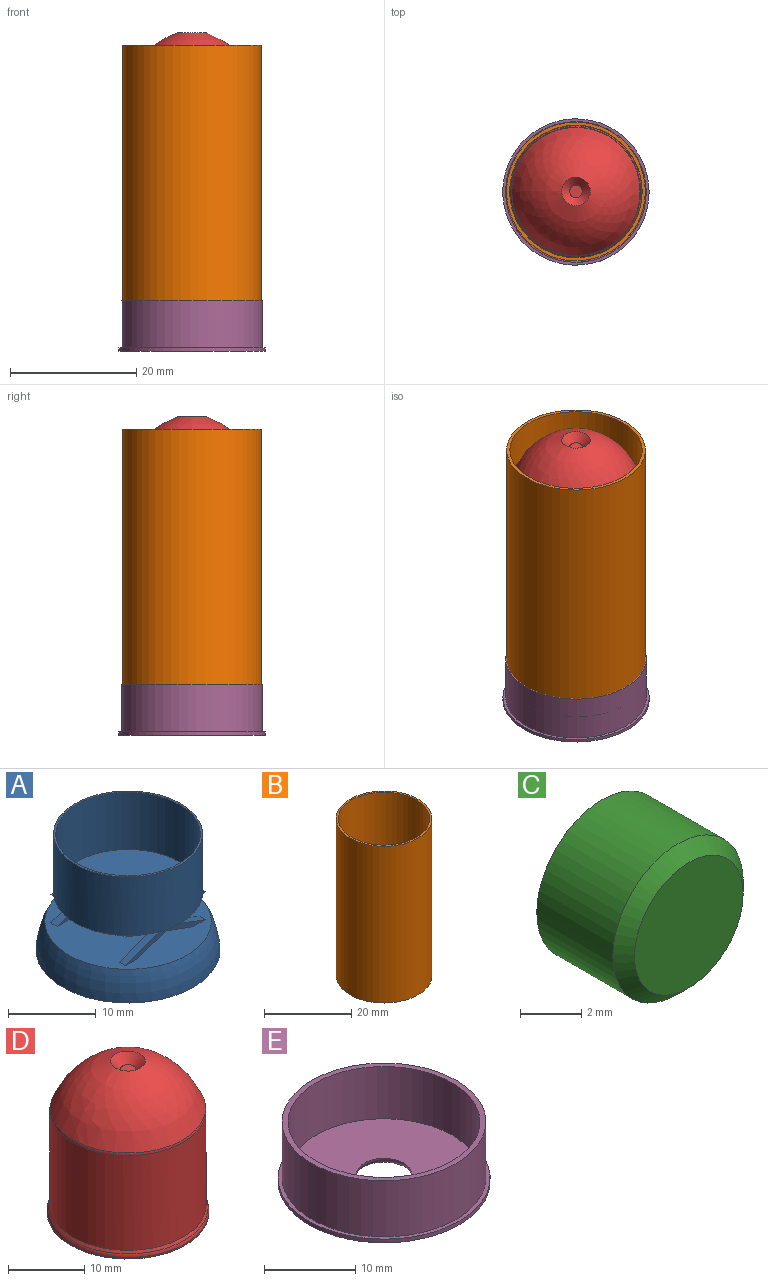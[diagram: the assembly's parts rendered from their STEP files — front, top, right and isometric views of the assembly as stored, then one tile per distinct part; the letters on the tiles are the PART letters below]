
ASSEMBLY  parts=5 mates=4
PART A: 40 faces, bbox 21x21x16.2 mm
  f0: plane 17.01x17.01mm, normal (0,0,-1), area 219.3mm2, adj f1,f6,f7,f8,f9,f10,f11,f12
  f1: cylinder r=8.5mm len=17mm, axis (0,0,1), area 437.9mm2, adj f0,f2,f3,f4,f5,f37
  f2: plane 0.45x0.43mm, normal (0,0,1), area 0.1mm2, adj f1,f8,f21
  f3: plane 0.45x0.43mm, normal (0,0,1), area 0.1mm2, adj f1,f8,f18
  f4: plane 0.46x0.43mm, normal (0,0,1), area 0.1mm2, adj f1,f12,f25
  f5: plane 0.45x0.43mm, normal (0,0,1), area 0.1mm2, adj f1,f12,f26
  f6: plane 4.43x1.63mm, normal (0.34,0,0.94), area 4.7mm2, adj f0,f7,f8,f9
  f7: plane 4.43x1.63mm, normal (-0.34,0,0.94), area 4.7mm2, adj f0,f6,f8,f9
  f8: plane 12.89x4mm, normal (0,1,0), area 15.2mm2, adj f0,f2,f3,f6,f7,f14,f17,f18
  f9: plane 12.9x4mm, normal (0,-1,0), area 14.8mm2, adj f0,f6,f7,f14,f17,f18,f19,f20
  f10: plane 4.43x1.63mm, normal (-0.34,0,0.94), area 4.7mm2, adj f0,f11,f12,f13
  f11: plane 4.43x1.63mm, normal (0.34,0,0.94), area 4.7mm2, adj f0,f10,f12,f13
  f12: plane 12.89x4mm, normal (0,-1,0), area 15.2mm2, adj f0,f4,f5,f10,f11,f14,f25,f26
  f13: plane 12.89x4mm, normal (0,1,0), area 14.8mm2, adj f0,f10,f11,f14,f25,f26,f27,f28
  f14: plane 19x18.95mm, normal (0,0,1), area 275.5mm2, adj f8,f9,f12,f13,f16,f17,f19,f20
  f15: plane 21x21mm, normal (0,0,-1), area 77.5mm2, adj f16,f23,f24,f35
  f16: torus R=0.21mm, axis (0,0,1), area 264.3mm2, adj f14,f15,f24
  f17: plane 5.45x2mm, normal (-0.34,0,0.94), area 5.8mm2, adj f8,f9,f14,f18
  f18: plane 5.46x2.01mm, normal (-0.34,0,-0.94), area 5.8mm2, adj f0,f3,f8,f9,f17
  f19: plane 4.45x1.63mm, normal (-0.34,0,-0.94), area 4.7mm2, adj f8,f9,f14,f20
  f20: plane 4.45x1.63mm, normal (0.34,0,-0.94), area 4.7mm2, adj f8,f9,f14,f19
  f21: plane 5.45x2mm, normal (0.34,0,-0.94), area 5.8mm2, adj f0,f2,f8,f9,f22
  f22: plane 5.45x2mm, normal (0.34,0,0.94), area 5.8mm2, adj f8,f9,f14,f21
  f23: plane 4x2mm, normal (1,0,0), area 8mm2, adj f14,f15,f24
  f24: cylinder r=9.5mm len=4mm, axis (0,0,1), area 8mm2, adj f15,f16,f23
  f25: plane 5.46x2.01mm, normal (0.34,0,-0.94), area 5.8mm2, adj f0,f4,f12,f13,f30
  f26: plane 5.45x2mm, normal (-0.34,0,-0.94), area 5.8mm2, adj f0,f5,f12,f13,f27
  f27: plane 5.45x2mm, normal (-0.34,0,0.94), area 5.8mm2, adj f12,f13,f14,f26
  f28: plane 4.45x1.63mm, normal (0.34,0,-0.94), area 4.7mm2, adj f12,f13,f14,f29
  f29: plane 4.45x1.63mm, normal (-0.34,0,-0.94), area 4.7mm2, adj f12,f13,f14,f28
  f30: plane 5.45x2mm, normal (0.34,0,0.94), area 5.8mm2, adj f12,f13,f14,f25
  f31: plane 10x1.01mm, normal (0,0,-1), area 10.1mm2, adj f9,f13,f32,f34
  f32: plane 10x0.45mm, normal (1,0,0), area 4.5mm2, adj f9,f13,f31,f33
  f33: plane 10x1.01mm, normal (0,0,1), area 10.1mm2, adj f9,f13,f32,f34
  f34: plane 10x0.45mm, normal (-1,0,0), area 4.5mm2, adj f9,f13,f31,f33
  f35: cylinder r=9.25mm len=18.5mm, axis (0,0,-1), area 116.2mm2, adj f15,f36
  f36: plane 18.5x18.5mm, normal (0,0,-1), area 268.8mm2, adj f35
  f37: plane 17x17mm, normal (0,0,1), area 13.2mm2, adj f1,f38
  f38: cylinder r=8.25mm len=16.5mm, axis (0,0,1), area 414.7mm2, adj f37,f39
  f39: plane 16.5x16.5mm, normal (0,0,1), area 213.8mm2, adj f38
PART B: 4 faces, bbox 22x22x44 mm
  f0: cylinder r=11mm len=44mm, axis (0,0,-1), area 3041.1mm2, adj f1,f2
  f1: plane 22x22mm, normal (0,0,1), area 33.8mm2, adj f0,f3
  f2: plane 22x22mm, normal (0,0,-1), area 33.8mm2, adj f0,f3
  f3: cylinder r=10.5mm len=44mm, axis (0,0,1), area 2902.8mm2, adj f1,f2
PART C: 4 faces, bbox 6x4x6 mm
  f0: cylinder r=3mm len=6mm, axis (0,1,0), area 66mm2, adj f2,f3
  f1: plane 5x5mm, normal (0,-1,0), area 19.6mm2, adj f2
  f2: cone r=2.5mm half-angle=45deg, axis (0,1,0), area 12.2mm2, adj f0,f1
  f3: plane 6x6mm, normal (0,1,0), area 28.3mm2, adj f0
PART D: 9 faces, bbox 22.9x22.9x24.3 mm
  f0: plane 21.2x21.2mm, normal (0,0,-1), area 353mm2, adj f1
  f1: cylinder r=10.6mm len=21.2mm, axis (0,0,-1), area 15.5mm2, adj f0,f5
  f2: cone r=10.6mm half-angle=30deg, axis (0,0,-1), area 30.2mm2, adj f3,f5
  f3: cylinder r=10.23mm len=20.47mm, axis (0,0,-1), area 978.3mm2, adj f2,f6
  f4: revolved ~20.34x20.34mm, area 481.3mm2, adj f6,f8
  f5: torus R=9.6mm, axis (0,0,1), area 34.7mm2, adj f1,f2
  f6: torus R=9.23mm, axis (0,0,1), area 23.5mm2, adj f3,f4
  f7: plane 2x2mm, normal (0,0,1), area 3.1mm2, adj f8
  f8: cone r=3mm half-angle=45deg, axis (0,0,1), area 18.4mm2, adj f4,f7
PART E: 8 faces, bbox 23.2x23.2x8 mm
  f0: plane 23.2x23.2mm, normal (0,0,-1), area 372.5mm2, adj f1,f6
  f1: cylinder r=11.6mm len=23.2mm, axis (0,0,1), area 36.4mm2, adj f0,f2
  f2: plane 23.2x23.2mm, normal (0,0,1), area 32.2mm2, adj f1,f3
  f3: cylinder r=11.15mm len=22.3mm, axis (0,0,1), area 525.4mm2, adj f2,f7
  f4: cylinder r=10.5mm len=21mm, axis (0,0,1), area 461.8mm2, adj f5,f7
  f5: plane 21x21mm, normal (0,0,1), area 318.1mm2, adj f4,f6
  f6: torus R=4mm, axis (0,0,1), area 33.2mm2, adj f0,f5
  f7: plane 22.3x22.3mm, normal (0,0,1), area 44.2mm2, adj f3,f4
PLACE A t=(-7.2,-8.1,-0.92)mm
PLACE B rot(axis=(1,0,0),180deg) t=(-7.2,-8.1,34.58)mm
PLACE C rot(axis=(-1,0,0),90deg) t=(-7.2,-8.1,-10.62)mm
PLACE D t=(-7.2,-8.1,22.38)mm
PLACE E t=(-7.2,-8.1,5.39)mm
MATE fastened D.f1 <-> A.f38  axis (0,0,-1) through (-7.2,-8.1,12.28)mm
MATE fastened B.f3 <-> E.f4  axis (0,0,-1) through (-7.2,-8.1,-9.42)mm
MATE fastened A.f35 <-> E.f4  axis (0,0,-1) through (-7.2,-8.1,-4.92)mm
MATE fastened C.f0 <-> E.f6  axis (0,0,-1) through (-7.2,-8.1,-13.62)mm
